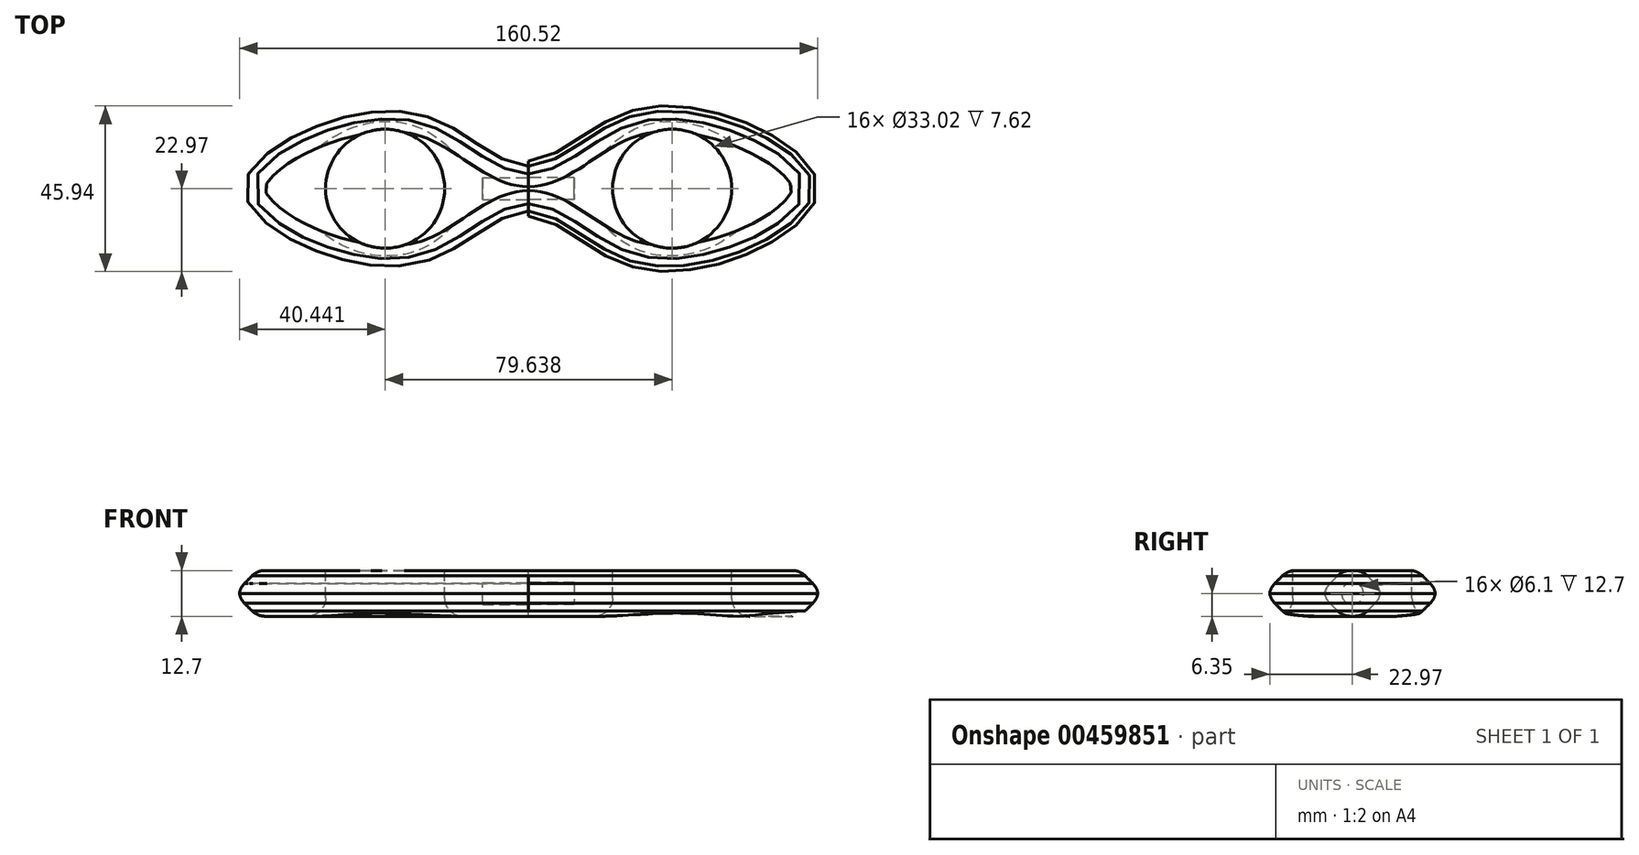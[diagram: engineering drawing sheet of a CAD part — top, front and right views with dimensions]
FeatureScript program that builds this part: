
annotation { "Feature Type Name" : "Feature", "Feature Type Description" : "" }
export const myFeature = defineFeature(function(context is Context, id is Id, definition is map)
    precondition{}
    {
        {
            var Q0;
            Q0=qCreatedBy(makeId("Top.planeOp"),FACE);
            var sketch = newSketch(context, id + "F0", { "sketchPlane" : qUnion([Q0])});
            skLineSegment(sketch, "E0.bottom", {"start": v(-76.92, 22.27) * mm, "end": v(76.92, 22.27) * mm, "construction": true});
            skLineSegment(sketch, "E0.top", {"start": v(-76.92, -22.27) * mm, "end": v(76.92, -22.27) * mm, "construction": true});
            skLineSegment(sketch, "E0.left", {"start": v(-76.92, 22.27) * mm, "end": v(-76.92, -22.27) * mm, "construction": true});
            skLineSegment(sketch, "E0.right", {"start": v(76.92, 22.27) * mm, "end": v(76.92, -22.27) * mm, "construction": true});
            skPoint(sketch, "E0.middle", {"position": v(0, 0) * mm});
            skLineSegment(sketch, "E1.bottom", {"start": v(-76.92, 7.72) * mm, "end": v(76.92, 7.72) * mm, "construction": true});
            skLineSegment(sketch, "E1.top", {"start": v(-76.92, -7.72) * mm, "end": v(76.92, -7.72) * mm, "construction": true});
            skLineSegment(sketch, "E1.left", {"start": v(-76.92, 7.72) * mm, "end": v(-76.92, -7.72) * mm, "construction": true});
            skLineSegment(sketch, "E1.right", {"start": v(76.92, 7.72) * mm, "end": v(76.92, -7.72) * mm, "construction": true});
            skLineSegment(sketch, "E2.bottom", {"start": v(30.74, 22.27) * mm, "end": v(-30.74, 22.27) * mm, "construction": true});
            skLineSegment(sketch, "E2.top", {"start": v(30.74, -22.27) * mm, "end": v(-30.74, -22.27) * mm, "construction": true});
            skLineSegment(sketch, "E2.left", {"start": v(30.74, 22.27) * mm, "end": v(30.74, -22.27) * mm, "construction": true});
            skLineSegment(sketch, "E2.right", {"start": v(-30.74, 22.27) * mm, "end": v(-30.74, -22.27) * mm, "construction": true});
            skFitSpline(sketch, "E3", {"points": [v(-76.92, 7.72) * mm, v(-30.74, 22.27) * mm, v(0, 7.72) * mm, v(30.74, 22.27) * mm, v(76.92, 7.72) * mm, v(76.92, -7.72) * mm, v(30.74, -22.27) * mm, v(0, -7.72) * mm, v(-30.74, -22.27) * mm, v(-76.92, -7.72) * mm, v(-76.92, 7.72) * mm]});
            skLineSegment(sketch, "E4", {"start": v(0, 7.72) * mm, "end": v(0, -7.72) * mm});
            skSolve(sketch);
        }
        {
            var Q0;
            {var subQ0=sQuery(id+"F0.wireOp",EDGE,"E4");Q0=makeQuery(id+"F0.imprint","IMPRINT",FACE,{"disambiguationData":[TD([[makeQuery(id+"F0.imprint","IMPRINT",EDGE,{"derivedFrom":subQ0}),-1.0]])]});}
            extrude(context, id + "F1", {"entities" : qUnion([Q0]), "depth" : 12.7 * mm});
        }
        {
            var Q0;
            {var subQ0=sQuery(id+"F0.wireOp",EDGE,"E4");Q0=makeQuery(id+"F0.imprint","IMPRINT",FACE,{"disambiguationData":[TD([[makeQuery(id+"F0.imprint","IMPRINT",EDGE,{"derivedFrom":subQ0}),1.0]])]});}
            extrude(context, id + "F2", {"entities" : qUnion([Q0]), "depth" : 12.7 * mm});
        }
        {
            var Q0;
            Q0=makeQuery(id+"F1.opExtrude","CAP_FACE",FACE,{"disambiguationData":[OSD([sQuery(id+"F0.wireOp",EDGE,"E3"),sQuery(id+"F0.wireOp",EDGE,"E4")])],"isStart":false});
            var sketch = newSketch(context, id + "F3", { "sketchPlane" : qUnion([Q0])});
            skLineSegment(sketch, "E5", {"start": v(0, 50.05) * mm, "end": v(0, -54.86) * mm, "construction": true});
            skCircle(sketch, "E6", {"center": v(-39.82, 0) * mm, "radius": 16.51 * mm});
            skCircle(sketch, "E7.MirrorC", {"center": v(39.82, 0) * mm, "radius": 16.51 * mm});
            skSolve(sketch);
        }
        {
            var Q0;
            Q0 = qSketchRegion(id + "F3", true);
            extrude(context, id + "F4", {"entities" : qUnion([Q0]), "operationType" : NewBodyOperationType.REMOVE, "endBound" : BoundingType.THROUGH_ALL, "oppositeDirection" : true, "depth" : 25.4 * mm});
        }
        {
            var Q0;
            Q0=makeQuery(id+"F1.opExtrude","CAP_EDGE",EDGE,{"disambiguationData":[OSD([sQuery(id+"F0.wireOp",EDGE,"E3")])],"isStart":false});
            chamfer(context, id + "F5", {"entities" : qUnion([Q0]), "width" : 5.08 * mm, "tangentPropagation" : true});
        }
        {
            var Q0;
            {var subQ0=sQuery(id+"F0.wireOp",EDGE,"E3");Q0=makeQuery(id+"F5.opChamfer","BLEND_EDGE",EDGE,{"blendedFrom":[makeQuery(id+"F1.opExtrude","CAP_EDGE",EDGE,{"disambiguationData":[OSD([subQ0])],"isStart":false}),makeQuery(id+"F1.opExtrude","SWEPT_FACE",FACE,{"disambiguationData":[OSD([subQ0])]})],"blendedInto":[makeQuery(id+"F1.opExtrude","SWEPT_FACE",FACE,{"disambiguationData":[OSD([subQ0])]})]});}
            var Q1;
            {var subQ0=sQuery(id+"F0.wireOp",EDGE,"E3");Q1=makeQuery(id+"F5.opChamfer","BLEND_EDGE",EDGE,{"blendedFrom":[makeQuery(id+"F1.opExtrude","CAP_EDGE",EDGE,{"disambiguationData":[OSD([subQ0])],"isStart":false}),makeQuery(id+"F1.opExtrude","CAP_FACE",FACE,{"disambiguationData":[OSD([subQ0,sQuery(id+"F0.wireOp",EDGE,"E4")])],"isStart":false})],"blendedInto":[makeQuery(id+"F1.opExtrude","CAP_FACE",FACE,{"disambiguationData":[OSD([subQ0,sQuery(id+"F0.wireOp",EDGE,"E4")])],"isStart":false})]});}
            var Q2;
            Q2=makeQuery(id+"F4.boolean.opBoolean","COPY",EDGE,{"derivedFrom":makeQuery(id+"F4.opExtrude","CAP_EDGE",EDGE,{"disambiguationData":[OSD([sQuery(id+"F3.wireOp",EDGE,"E6")])],"isStart":true})});
            fillet(context, id + "F6", {"entities" : qUnion([Q0, Q1, Q2]), "radius" : 5.08 * mm, "tangentPropagation" : true, "allowEdgeOverflow" : false});
        }
        {
            var Q0;
            Q0=makeQuery(id+"F2.opExtrude","CAP_EDGE",EDGE,{"disambiguationData":[OSD([sQuery(id+"F0.wireOp",EDGE,"E3")])],"isStart":false});
            chamfer(context, id + "F7", {"entities" : qUnion([Q0]), "width" : 5.08 * mm, "tangentPropagation" : true});
        }
        {
            var Q0;
            {var subQ0=sQuery(id+"F0.wireOp",EDGE,"E3");Q0=makeQuery(id+"F7.opChamfer","BLEND_EDGE",EDGE,{"blendedFrom":[makeQuery(id+"F2.opExtrude","CAP_EDGE",EDGE,{"disambiguationData":[OSD([subQ0])],"isStart":false}),makeQuery(id+"F2.opExtrude","SWEPT_FACE",FACE,{"disambiguationData":[OSD([subQ0])]})],"blendedInto":[makeQuery(id+"F2.opExtrude","SWEPT_FACE",FACE,{"disambiguationData":[OSD([subQ0])]})]});}
            var Q1;
            Q1=makeQuery(id+"F4.boolean.opBoolean","COPY",EDGE,{"derivedFrom":makeQuery(id+"F4.opExtrude","CAP_EDGE",EDGE,{"disambiguationData":[OSD([sQuery(id+"F3.wireOp",EDGE,"E7.MirrorC")])],"isStart":true})});
            var Q2;
            {var subQ0=sQuery(id+"F0.wireOp",EDGE,"E3");Q2=makeQuery(id+"F7.opChamfer","BLEND_EDGE",EDGE,{"blendedFrom":[makeQuery(id+"F2.opExtrude","CAP_EDGE",EDGE,{"disambiguationData":[OSD([subQ0])],"isStart":false}),makeQuery(id+"F2.opExtrude","CAP_FACE",FACE,{"disambiguationData":[OSD([subQ0,sQuery(id+"F0.wireOp",EDGE,"E4")])],"isStart":false})],"blendedInto":[makeQuery(id+"F2.opExtrude","CAP_FACE",FACE,{"disambiguationData":[OSD([subQ0,sQuery(id+"F0.wireOp",EDGE,"E4")])],"isStart":false})]});}
            fillet(context, id + "F8", {"entities" : qUnion([Q0, Q1, Q2]), "radius" : 5.08 * mm, "tangentPropagation" : true, "allowEdgeOverflow" : false});
        }
        {
            var Q0;
            Q0=makeQuery(id+"F1.opExtrude","CAP_EDGE",EDGE,{"disambiguationData":[OSD([sQuery(id+"F0.wireOp",EDGE,"E3")])],"isStart":true});
            var Q1;
            Q1=makeQuery(id+"F2.opExtrude","CAP_EDGE",EDGE,{"disambiguationData":[OSD([sQuery(id+"F0.wireOp",EDGE,"E3")])],"isStart":true});
            chamfer(context, id + "F9", {"entities" : qUnion([Q0, Q1]), "width" : 5.08 * mm, "tangentPropagation" : true});
        }
        {
            var Q0;
            {var subQ0=sQuery(id+"F0.wireOp",EDGE,"E3");Q0=makeQuery(id+"F9.opChamfer","BLEND_EDGE",EDGE,{"blendedFrom":[makeQuery(id+"F1.opExtrude","CAP_EDGE",EDGE,{"disambiguationData":[OSD([subQ0])],"isStart":true}),makeQuery(id+"F1.opExtrude","SWEPT_FACE",FACE,{"disambiguationData":[OSD([subQ0])]})],"blendedInto":[makeQuery(id+"F1.opExtrude","SWEPT_FACE",FACE,{"disambiguationData":[OSD([subQ0])]})]});}
            var Q1;
            {var subQ0=sQuery(id+"F0.wireOp",EDGE,"E3");Q1=makeQuery(id+"F9.opChamfer","BLEND_EDGE",EDGE,{"blendedFrom":[makeQuery(id+"F2.opExtrude","CAP_EDGE",EDGE,{"disambiguationData":[OSD([subQ0])],"isStart":true}),makeQuery(id+"F2.opExtrude","SWEPT_FACE",FACE,{"disambiguationData":[OSD([subQ0])]})],"blendedInto":[makeQuery(id+"F2.opExtrude","SWEPT_FACE",FACE,{"disambiguationData":[OSD([subQ0])]})]});}
            var Q2;
            {var subQ0=sQuery(id+"F0.wireOp",EDGE,"E3");Q2=makeQuery(id+"F9.opChamfer","BLEND_EDGE",EDGE,{"blendedFrom":[makeQuery(id+"F1.opExtrude","CAP_EDGE",EDGE,{"disambiguationData":[OSD([subQ0])],"isStart":true}),makeQuery(id+"F1.opExtrude","CAP_FACE",FACE,{"disambiguationData":[OSD([subQ0,sQuery(id+"F0.wireOp",EDGE,"E4")])],"isStart":true})],"blendedInto":[makeQuery(id+"F1.opExtrude","CAP_FACE",FACE,{"disambiguationData":[OSD([subQ0,sQuery(id+"F0.wireOp",EDGE,"E4")])],"isStart":true})]});}
            var Q3;
            {var subQ0=sQuery(id+"F0.wireOp",EDGE,"E3");Q3=makeQuery(id+"F9.opChamfer","BLEND_EDGE",EDGE,{"blendedFrom":[makeQuery(id+"F2.opExtrude","CAP_EDGE",EDGE,{"disambiguationData":[OSD([subQ0])],"isStart":true}),makeQuery(id+"F2.opExtrude","CAP_FACE",FACE,{"disambiguationData":[OSD([subQ0,sQuery(id+"F0.wireOp",EDGE,"E4")])],"isStart":true})],"blendedInto":[makeQuery(id+"F2.opExtrude","CAP_FACE",FACE,{"disambiguationData":[OSD([subQ0,sQuery(id+"F0.wireOp",EDGE,"E4")])],"isStart":true})]});}
            var Q4;
            Q4=makeQuery(id+"F4.boolean.opBoolean","INTERSECT",EDGE,{"derivedFrom":[makeQuery(id+"F2.opExtrude","CAP_FACE",FACE,{"disambiguationData":[OSD([sQuery(id+"F0.wireOp",EDGE,"E3"),sQuery(id+"F0.wireOp",EDGE,"E4")])],"isStart":true}),makeQuery(id+"F4.opExtrude","SWEPT_FACE",FACE,{"disambiguationData":[OSD([sQuery(id+"F3.wireOp",EDGE,"E7.MirrorC")])]})]});
            var Q5;
            Q5=makeQuery(id+"F4.boolean.opBoolean","INTERSECT",EDGE,{"derivedFrom":[makeQuery(id+"F1.opExtrude","CAP_FACE",FACE,{"disambiguationData":[OSD([sQuery(id+"F0.wireOp",EDGE,"E3"),sQuery(id+"F0.wireOp",EDGE,"E4")])],"isStart":true}),makeQuery(id+"F4.opExtrude","SWEPT_FACE",FACE,{"disambiguationData":[OSD([sQuery(id+"F3.wireOp",EDGE,"E6")])]})]});
            fillet(context, id + "F10", {"entities" : qUnion([Q0, Q1, Q2, Q3, Q4, Q5]), "radius" : 5.08 * mm, "tangentPropagation" : true, "allowEdgeOverflow" : false});
        }
        {
            var Q0;
            Q0=makeQuery(id+"F1.opExtrude","SWEPT_FACE",FACE,{"disambiguationData":[OSD([sQuery(id+"F0.wireOp",EDGE,"E4")])]});
            var sketch = newSketch(context, id + "F11", { "sketchPlane" : qUnion([Q0])});
            skCircle(sketch, "E8", {"center": v(0, 6.35) * mm, "radius": 3.05 * mm});
            skSolve(sketch);
        }
        {
            var Q0;
            Q0 = qSketchRegion(id + "F11", true);
            extrude(context, id + "F12", {"entities" : qUnion([Q0]), "operationType" : NewBodyOperationType.REMOVE, "oppositeDirection" : true, "depth" : 12.7 * mm});
        }
        {
            var Q0;
            Q0=makeQuery(id+"F2.opExtrude","SWEPT_FACE",FACE,{"disambiguationData":[OSD([sQuery(id+"F0.wireOp",EDGE,"E4")])]});
            var sketch = newSketch(context, id + "F13", { "sketchPlane" : qUnion([Q0])});
            skCircle(sketch, "E9", {"center": v(0, 6.35) * mm, "radius": 3.05 * mm});
            skSolve(sketch);
        }
        {
            var Q0;
            Q0 = qSketchRegion(id + "F13", true);
            extrude(context, id + "F14", {"entities" : qUnion([Q0]), "operationType" : NewBodyOperationType.REMOVE, "oppositeDirection" : true, "depth" : 12.7 * mm});
        }
    });
